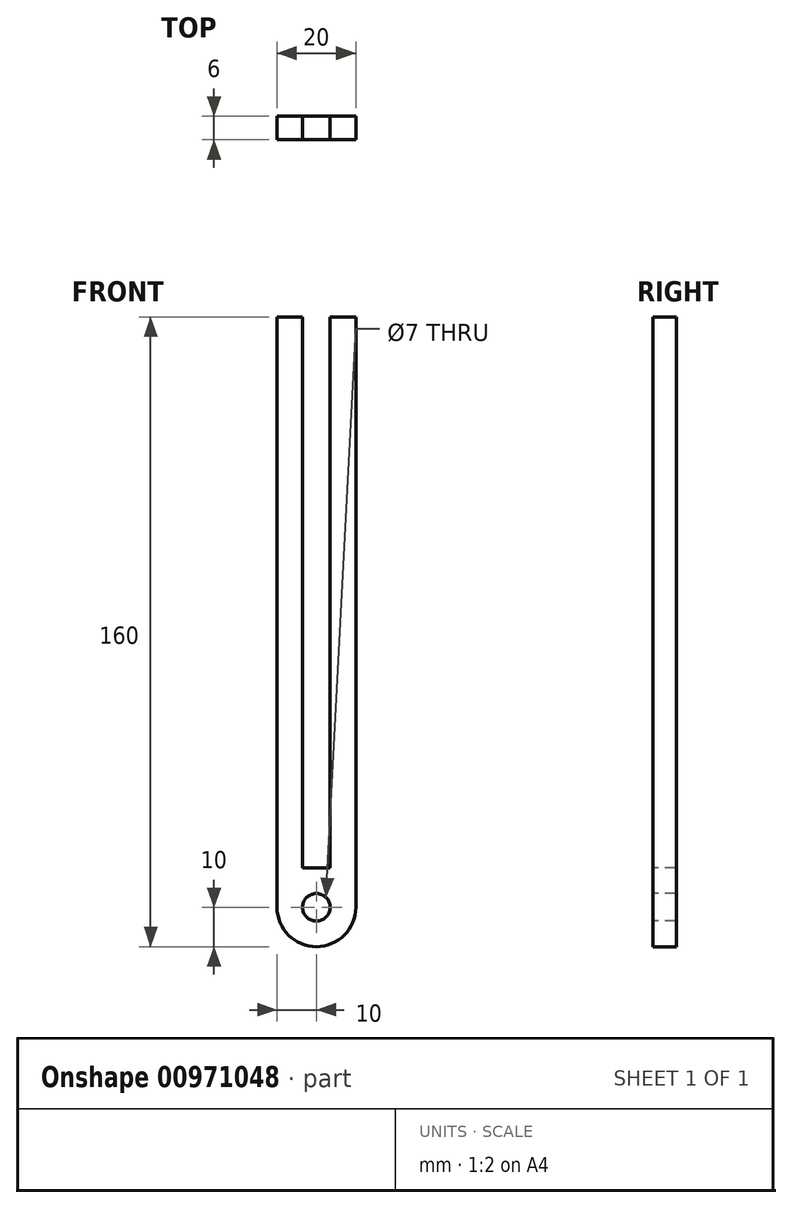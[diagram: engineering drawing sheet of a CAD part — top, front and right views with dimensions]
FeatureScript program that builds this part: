
annotation { "Feature Type Name" : "Feature", "Feature Type Description" : "" }
export const myFeature = defineFeature(function(context is Context, id is Id, definition is map)
    precondition{}
    {
        {
            var Q0;
            Q0=qCreatedBy(makeId("Front.planeOp"),FACE);
            var sketch = newSketch(context, id + "F0", { "sketchPlane" : qUnion([Q0])});
            skArc(sketch, "E0", {"start": v(-10, 0) * mm, "mid": v(0, -10) * mm, "end": v(10, 0) * mm});
            skCircle(sketch, "E1", {"center": v(0, 0) * mm, "radius": 3.5 * mm});
            skLineSegment(sketch, "E2.bottom", {"start": v(10, 150) * mm, "end": v(-10, 150) * mm});
            skLineSegment(sketch, "E2.left", {"start": v(10, 150) * mm, "end": v(10, 0) * mm});
            skLineSegment(sketch, "E2.right", {"start": v(-10, 150) * mm, "end": v(-10, 0) * mm});
            skSolve(sketch);
        }
        {
            var Q0;
            Q0=makeQuery(id+"F0.imprint","IMPRINT",FACE,{"disambiguationData":[TD([[makeQuery(id+"F0.imprint","IMPRINT",EDGE,{"derivedFrom":sQuery(id+"F0.wireOp",EDGE,"E0")}),1.0]])]});
            extrude(context, id + "F1", {"entities" : qUnion([Q0]), "oppositeDirection" : true, "depth" : 6 * mm, "offsetDistance" : 25 * mm});
        }
        {
            var Q0;
            Q0=makeQuery(id+"F0.imprint","IMPRINT",FACE,{"disambiguationData":[TD([[makeQuery(id+"F0.imprint","IMPRINT",EDGE,{"derivedFrom":sQuery(id+"F0.wireOp",EDGE,"E0")}),1.0]])]});
            var sketch = newSketch(context, id + "F2", { "sketchPlane" : qUnion([Q0])});
            skLineSegment(sketch, "E3.bottom", {"start": v(-3.5, 160) * mm, "end": v(3.5, 160) * mm});
            skLineSegment(sketch, "E3.top", {"start": v(-3.5, 10) * mm, "end": v(3.5, 10) * mm});
            skLineSegment(sketch, "E3.left", {"start": v(-3.5, 160) * mm, "end": v(-3.5, 10) * mm});
            skLineSegment(sketch, "E3.right", {"start": v(3.5, 160) * mm, "end": v(3.5, 10) * mm});
            skSolve(sketch);
        }
        {
            var Q0;
            Q0 = qSketchRegion(id + "F2", true);
            extrude(context, id + "F3", {"entities" : qUnion([Q0]), "operationType" : NewBodyOperationType.REMOVE, "oppositeDirection" : true, "depth" : 25 * mm, "offsetDistance" : 25 * mm});
        }
    });
